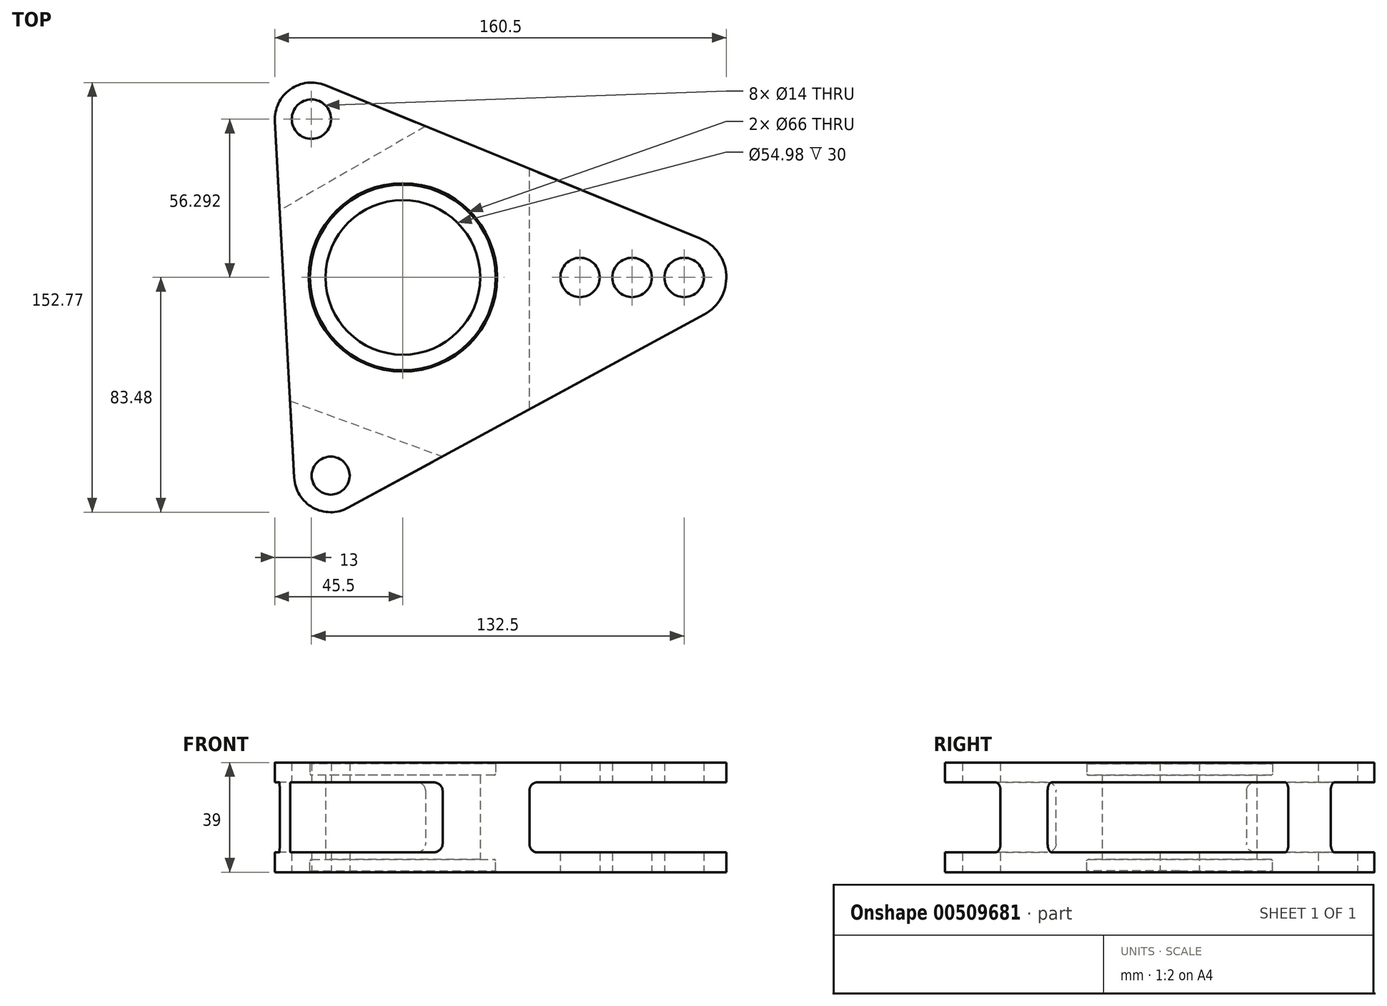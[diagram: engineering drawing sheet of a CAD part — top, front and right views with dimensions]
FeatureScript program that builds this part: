
annotation { "Feature Type Name" : "Feature", "Feature Type Description" : "" }
export const myFeature = defineFeature(function(context is Context, id is Id, definition is map)
    precondition{}
    {
        {
            var Q0;
            Q0=qCreatedBy(makeId("Top.planeOp"),FACE);
            var sketch = newSketch(context, id + "F0", { "sketchPlane" : qUnion([Q0])});
            skArc(sketch, "E0", {"start": v(107.16, -13.18) * mm, "mid": v(114.98, 0.82) * mm, "end": v(105.67, 13.89) * mm});
            skLineSegment(sketch, "E1", {"start": v(-32.5, 56.3) * mm, "end": v(0, 0) * mm, "construction": true});
            skLineSegment(sketch, "E2", {"start": v(0, 0) * mm, "end": v(100, 0) * mm, "construction": true});
            skLineSegment(sketch, "E3", {"start": v(107.16, -13.18) * mm, "end": v(-19.45, -81.9) * mm});
            skLineSegment(sketch, "E4", {"start": v(105.67, 13.89) * mm, "end": v(-27.58, 68.33) * mm});
            skCircle(sketch, "E5", {"center": v(0, 0) * mm, "radius": 27.49 * mm});
            skCircle(sketch, "E6", {"center": v(0, 0) * mm, "radius": 33 * mm});
            skCircle(sketch, "E7", {"center": v(-25.65, -70.48) * mm, "radius": 6.75 * mm});
            skCircle(sketch, "E8", {"center": v(100, 0) * mm, "radius": 7 * mm});
            skCircle(sketch, "E9", {"center": v(-32.5, 56.3) * mm, "radius": 7 * mm});
            skLineSegment(sketch, "E10", {"start": v(0, 0) * mm, "end": v(-25.65, -70.48) * mm, "construction": true});
            skCircle(sketch, "E11", {"center": v(81.5, 0) * mm, "radius": 7 * mm});
            skCircle(sketch, "E12", {"center": v(63, 0) * mm, "radius": 7 * mm});
            skArc(sketch, "E13", {"start": v(-27.58, 68.33) * mm, "mid": v(-40.04, 66.88) * mm, "end": v(-45.48, 55.6) * mm});
            skLineSegment(sketch, "E14", {"start": v(-38.63, -71.18) * mm, "end": v(-45.48, 55.6) * mm});
            skArc(sketch, "E15", {"start": v(-38.63, -71.18) * mm, "mid": v(-32, -81.82) * mm, "end": v(-19.45, -81.9) * mm});
            skSolve(sketch);
        }
        {
            var Q0;
            Q0=makeQuery(id+"F0.imprint","IMPRINT",FACE,{"disambiguationData":[TD([[makeQuery(id+"F0.imprint","IMPRINT",EDGE,{"derivedFrom":sQuery(id+"F0.wireOp",EDGE,"E0")}),1.0]])]});
            var Q1;
            Q1=makeQuery(id+"F0.imprint","IMPRINT",FACE,{"disambiguationData":[TD([[makeQuery(id+"F0.imprint","IMPRINT",EDGE,{"derivedFrom":sQuery(id+"F0.wireOp",EDGE,"E5")}),-1.0]])]});
            extrude(context, id + "F1", {"entities" : qUnion([Q0, Q1]), "depth" : (39 / 2) * mm, "hasSecondDirection" : true, "secondDirectionOppositeDirection" : true, "secondDirectionDepth" : (39 / 2) * mm, "offsetDistance" : 25 * mm});
        }
        {
            var Q0;
            Q0=makeQuery(id+"F0.imprint","IMPRINT",FACE,{"disambiguationData":[TD([[makeQuery(id+"F0.imprint","IMPRINT",EDGE,{"derivedFrom":sQuery(id+"F0.wireOp",EDGE,"E5")}),-1.0]])]});
            extrude(context, id + "F2", {"entities" : qUnion([Q0]), "depth" : 25 * mm, "hasSecondDirection" : true, "secondDirectionOppositeDirection" : false, "secondDirectionDepth" : 15 * mm});
        }
        {
            var Q0;
            Q0=makeQuery(id+"F2.opExtrude","SWEPT_BODY",BODY,{"disambiguationData":[OSD([sQuery(id+"F0.wireOp",EDGE,"E5"),sQuery(id+"F0.wireOp",EDGE,"E6")])]});
            var Q1;
            Q1=qCreatedBy(makeId("Top.planeOp"),FACE);
            mirror(context, id + "F3", {"entities" : qUnion([Q0]), "mirrorPlane" : qUnion([Q1])});
        }
        {
            var Q0;
            Q0=makeQuery(id+"F2.opExtrude","SWEPT_BODY",BODY,{"disambiguationData":[OSD([sQuery(id+"F0.wireOp",EDGE,"E5"),sQuery(id+"F0.wireOp",EDGE,"E6")])]});
            var Q1;
            Q1=makeQuery(id+"F3.opPattern","COPY",BODY,{"derivedFrom":makeQuery(id+"F2.opExtrude","SWEPT_BODY",BODY,{"disambiguationData":[OSD([sQuery(id+"F0.wireOp",EDGE,"E5"),sQuery(id+"F0.wireOp",EDGE,"E6")])]}),"instanceName":"1"});
            var Q2;
            Q2=makeQuery(id+"F1.opExtrude","SWEPT_BODY",BODY,{"disambiguationData":[OSD([sQuery(id+"F0.wireOp",EDGE,"D8dMaxUI-krC3-8Rgy-GWV3-kWU7Q4TT3Lab"),sQuery(id+"F0.wireOp",EDGE,"3Sw5jc8D-vO1D-bRZ2-Dp3C-G4mATATASSja"),sQuery(id+"F0.wireOp",EDGE,"E0"),sQuery(id+"F0.wireOp",EDGE,"zj2CIV8g-hFVo-fksV-1Kmp-BisU3r2Nm6Xd"),sQuery(id+"F0.wireOp",EDGE,"E3"),sQuery(id+"F0.wireOp",EDGE,"E4"),sQuery(id+"F0.wireOp",EDGE,"qkPLOzcV-Iwq5-aCvg-uIFe-w5CNodWGUBt3"),sQuery(id+"F0.wireOp",EDGE,"A7vblU06-5T2E-xFhw-Prem-bZOXUrPWXHlZ"),sQuery(id+"F0.wireOp",EDGE,"FWEk8V89-gh5E-MftK-NO6Q-vmILQQlNtGV9"),sQuery(id+"F0.wireOp",EDGE,"JZj7mYVi-bQwG-J3x1-Qx5E-SCilTMfAAKcG"),sQuery(id+"F0.wireOp",EDGE,"BdHZZvG3-k1rE-q5c3-X2zL-i16wHEfPjIDr"),sQuery(id+"F0.wireOp",EDGE,"aHxJ3uwQ-QgmQ-6vBI-lO01-pxuYQwz69qWK"),sQuery(id+"F0.wireOp",EDGE,"E5"),sQuery(id+"F0.wireOp",EDGE,"E7"),sQuery(id+"F0.wireOp",EDGE,"E8"),sQuery(id+"F0.wireOp",EDGE,"E9")])]});
            booleanBodies(context, id + "F4", {"operationType" : BooleanOperationType.SUBTRACTION, "tools" : qUnion([Q0, Q1]), "targets" : qUnion([Q2])});
        }
        {
            var Q0;
            Q0=qCreatedBy(makeId("Top.planeOp"),FACE);
            var sketch = newSketch(context, id + "F5", { "sketchPlane" : qUnion([Q0])});
            skLineSegment(sketch, "E16", {"start": v(233.15, 12.77) * mm, "end": v(-67, -150.15) * mm});
            skLineSegment(sketch, "E17", {"start": v(-82.77, 141.84) * mm, "end": v(233.15, 12.77) * mm});
            skLineSegment(sketch, "E18", {"start": v(-41.89, -7.2) * mm, "end": v(-41.89, -7.2) * mm});
            skLineSegment(sketch, "E19", {"start": v(-82.77, 141.84) * mm, "end": v(-67, -150.15) * mm});
            skLineSegment(sketch, "E20", {"start": v(45, -74.9) * mm, "end": v(45, 75.06) * mm});
            skLineSegment(sketch, "E21", {"start": v(45, 75.06) * mm, "end": v(-114.31, -16.92) * mm});
            skLineSegment(sketch, "E22", {"start": v(-114.31, -16.92) * mm, "end": v(45, -74.9) * mm});
            skLineSegment(sketch, "E23", {"start": v(0, 0) * mm, "end": v(100, 0) * mm, "construction": true});
            skSolve(sketch);
        }
        {
            var Q0;
            Q0=makeQuery(id+"F5.imprint","IMPRINT",FACE,{"disambiguationData":[TD([[makeQuery(id+"F5.imprint","IMPRINT",EDGE,{"derivedFrom":sQuery(id+"F5.wireOp",EDGE,"biPIagPa-8M9t-NqUM-etFK-JsX3kBdDWFOZ")}),-1.0]])]});
            var Q1;
            Q1=makeQuery(id+"F5.imprint","IMPRINT",FACE,{"disambiguationData":[TD([[makeQuery(id+"F5.imprint","IMPRINT",EDGE,{"derivedFrom":sQuery(id+"F5.wireOp",EDGE,"oxfCw9Kj-M5LM-K66p-6C1q-elJlnXFWBCB9")}),1.0]])]});
            var Q2;
            Q2=makeQuery(id+"F5.imprint","IMPRINT",FACE,{"disambiguationData":[TD([[makeQuery(id+"F5.imprint","IMPRINT",EDGE,{"derivedFrom":sQuery(id+"F5.wireOp",EDGE,"E16")}),-1.0]])]});
            extrude(context, id + "F6", {"entities" : qUnion([Q0, Q1, Q2]), "operationType" : NewBodyOperationType.REMOVE, "oppositeDirection" : true, "depth" : 12.5 * mm, "hasSecondDirection" : true, "secondDirectionOppositeDirection" : false, "secondDirectionDepth" : 12.5 * mm});
        }
        {
            var Q0;
            Q0=makeQuery(id+"F6.boolean.opBoolean","COPY",EDGE,{"derivedFrom":makeQuery(id+"F6.opExtrude","CAP_EDGE",EDGE,{"disambiguationData":[OSD([sQuery(id+"F5.wireOp",EDGE,"E20")])],"isStart":false})});
            var Q1;
            Q1=makeQuery(id+"F6.boolean.opBoolean","COPY",EDGE,{"derivedFrom":makeQuery(id+"F6.opExtrude","CAP_EDGE",EDGE,{"disambiguationData":[OSD([sQuery(id+"F5.wireOp",EDGE,"E21")])],"isStart":false})});
            var Q2;
            Q2=makeQuery(id+"F6.boolean.opBoolean","COPY",EDGE,{"derivedFrom":makeQuery(id+"F6.opExtrude","CAP_EDGE",EDGE,{"disambiguationData":[OSD([sQuery(id+"F5.wireOp",EDGE,"E21")])],"isStart":true})});
            var Q3;
            Q3=makeQuery(id+"F6.boolean.opBoolean","COPY",EDGE,{"derivedFrom":makeQuery(id+"F6.opExtrude","CAP_EDGE",EDGE,{"disambiguationData":[OSD([sQuery(id+"F5.wireOp",EDGE,"E20")])],"isStart":true})});
            var Q4;
            Q4=makeQuery(id+"F6.boolean.opBoolean","COPY",EDGE,{"derivedFrom":makeQuery(id+"F6.opExtrude","CAP_EDGE",EDGE,{"disambiguationData":[OSD([sQuery(id+"F5.wireOp",EDGE,"E22")])],"isStart":true})});
            var Q5;
            Q5=makeQuery(id+"F6.boolean.opBoolean","COPY",EDGE,{"derivedFrom":makeQuery(id+"F6.opExtrude","CAP_EDGE",EDGE,{"disambiguationData":[OSD([sQuery(id+"F5.wireOp",EDGE,"E22")])],"isStart":false})});
            fillet(context, id + "F7", {"entities" : qUnion([Q0, Q1, Q2, Q3, Q4, Q5]), "radius" : 3 * mm, "tangentPropagation" : true, "defaultsChanged" : true, "vertexSettings" : [], "allowEdgeOverflow" : false});
        }
        {
            var Q0;
            Q0=makeQuery(id+"F4.opBoolean","COPY",EDGE,{"derivedFrom":makeQuery(id+"F2.opExtrude","CAP_EDGE",EDGE,{"disambiguationData":[OSD([sQuery(id+"F0.wireOp",EDGE,"E5")])],"isStart":true})});
            var Q1;
            Q1=makeQuery(id+"F4.opBoolean","COPY",EDGE,{"derivedFrom":makeQuery(id+"F3.opPattern","COPY",EDGE,{"derivedFrom":makeQuery(id+"F2.opExtrude","CAP_EDGE",EDGE,{"disambiguationData":[OSD([sQuery(id+"F0.wireOp",EDGE,"E5")])],"isStart":true}),"instanceName":"1"})});
            var Q2;
            Q2=makeQuery(id+"F4.opBoolean","INTERSECT",EDGE,{"derivedFrom":[makeQuery(id+"F1.opExtrude","CAP_FACE",FACE,{"disambiguationData":[OSD([sQuery(id+"F0.wireOp",EDGE,"D8dMaxUI-krC3-8Rgy-GWV3-kWU7Q4TT3Lab"),sQuery(id+"F0.wireOp",EDGE,"3Sw5jc8D-vO1D-bRZ2-Dp3C-G4mATATASSja"),sQuery(id+"F0.wireOp",EDGE,"E0"),sQuery(id+"F0.wireOp",EDGE,"zj2CIV8g-hFVo-fksV-1Kmp-BisU3r2Nm6Xd"),sQuery(id+"F0.wireOp",EDGE,"E3"),sQuery(id+"F0.wireOp",EDGE,"E4"),sQuery(id+"F0.wireOp",EDGE,"qkPLOzcV-Iwq5-aCvg-uIFe-w5CNodWGUBt3"),sQuery(id+"F0.wireOp",EDGE,"A7vblU06-5T2E-xFhw-Prem-bZOXUrPWXHlZ"),sQuery(id+"F0.wireOp",EDGE,"FWEk8V89-gh5E-MftK-NO6Q-vmILQQlNtGV9"),sQuery(id+"F0.wireOp",EDGE,"JZj7mYVi-bQwG-J3x1-Qx5E-SCilTMfAAKcG"),sQuery(id+"F0.wireOp",EDGE,"BdHZZvG3-k1rE-q5c3-X2zL-i16wHEfPjIDr"),sQuery(id+"F0.wireOp",EDGE,"aHxJ3uwQ-QgmQ-6vBI-lO01-pxuYQwz69qWK"),sQuery(id+"F0.wireOp",EDGE,"E5"),sQuery(id+"F0.wireOp",EDGE,"E7"),sQuery(id+"F0.wireOp",EDGE,"E8"),sQuery(id+"F0.wireOp",EDGE,"E9")])],"isStart":false}),makeQuery(id+"F2.opExtrude","SWEPT_FACE",FACE,{"disambiguationData":[OSD([sQuery(id+"F0.wireOp",EDGE,"E6")])]})]});
            var Q3;
            Q3=makeQuery(id+"F4.opBoolean","INTERSECT",EDGE,{"derivedFrom":[makeQuery(id+"F1.opExtrude","CAP_FACE",FACE,{"disambiguationData":[OSD([sQuery(id+"F0.wireOp",EDGE,"D8dMaxUI-krC3-8Rgy-GWV3-kWU7Q4TT3Lab"),sQuery(id+"F0.wireOp",EDGE,"3Sw5jc8D-vO1D-bRZ2-Dp3C-G4mATATASSja"),sQuery(id+"F0.wireOp",EDGE,"E0"),sQuery(id+"F0.wireOp",EDGE,"zj2CIV8g-hFVo-fksV-1Kmp-BisU3r2Nm6Xd"),sQuery(id+"F0.wireOp",EDGE,"E3"),sQuery(id+"F0.wireOp",EDGE,"E4"),sQuery(id+"F0.wireOp",EDGE,"qkPLOzcV-Iwq5-aCvg-uIFe-w5CNodWGUBt3"),sQuery(id+"F0.wireOp",EDGE,"A7vblU06-5T2E-xFhw-Prem-bZOXUrPWXHlZ"),sQuery(id+"F0.wireOp",EDGE,"FWEk8V89-gh5E-MftK-NO6Q-vmILQQlNtGV9"),sQuery(id+"F0.wireOp",EDGE,"JZj7mYVi-bQwG-J3x1-Qx5E-SCilTMfAAKcG"),sQuery(id+"F0.wireOp",EDGE,"BdHZZvG3-k1rE-q5c3-X2zL-i16wHEfPjIDr"),sQuery(id+"F0.wireOp",EDGE,"aHxJ3uwQ-QgmQ-6vBI-lO01-pxuYQwz69qWK"),sQuery(id+"F0.wireOp",EDGE,"E5"),sQuery(id+"F0.wireOp",EDGE,"E7"),sQuery(id+"F0.wireOp",EDGE,"E8"),sQuery(id+"F0.wireOp",EDGE,"E9")])],"isStart":true}),makeQuery(id+"F3.opPattern","COPY",FACE,{"derivedFrom":makeQuery(id+"F2.opExtrude","SWEPT_FACE",FACE,{"disambiguationData":[OSD([sQuery(id+"F0.wireOp",EDGE,"E6")])]}),"instanceName":"1"})]});
            chamfer(context, id + "F8", {"entities" : qUnion([Q0, Q1, Q2, Q3]), "width" : 0.5 * mm, "tangentPropagation" : true});
        }
        {
            var Q0;
            Q0=makeQuery(id+"F4.opBoolean","COPY",EDGE,{"derivedFrom":makeQuery(id+"F3.opPattern","COPY",EDGE,{"derivedFrom":makeQuery(id+"F2.opExtrude","CAP_EDGE",EDGE,{"disambiguationData":[OSD([sQuery(id+"F0.wireOp",EDGE,"E6")])],"isStart":true}),"instanceName":"1"})});
            var Q1;
            Q1=makeQuery(id+"F4.opBoolean","COPY",EDGE,{"derivedFrom":makeQuery(id+"F2.opExtrude","CAP_EDGE",EDGE,{"disambiguationData":[OSD([sQuery(id+"F0.wireOp",EDGE,"E6")])],"isStart":true})});
            fillet(context, id + "F9", {"entities" : qUnion([Q0, Q1]), "radius" : 0.5 * mm, "tangentPropagation" : true, "allowEdgeOverflow" : false});
        }
    });
